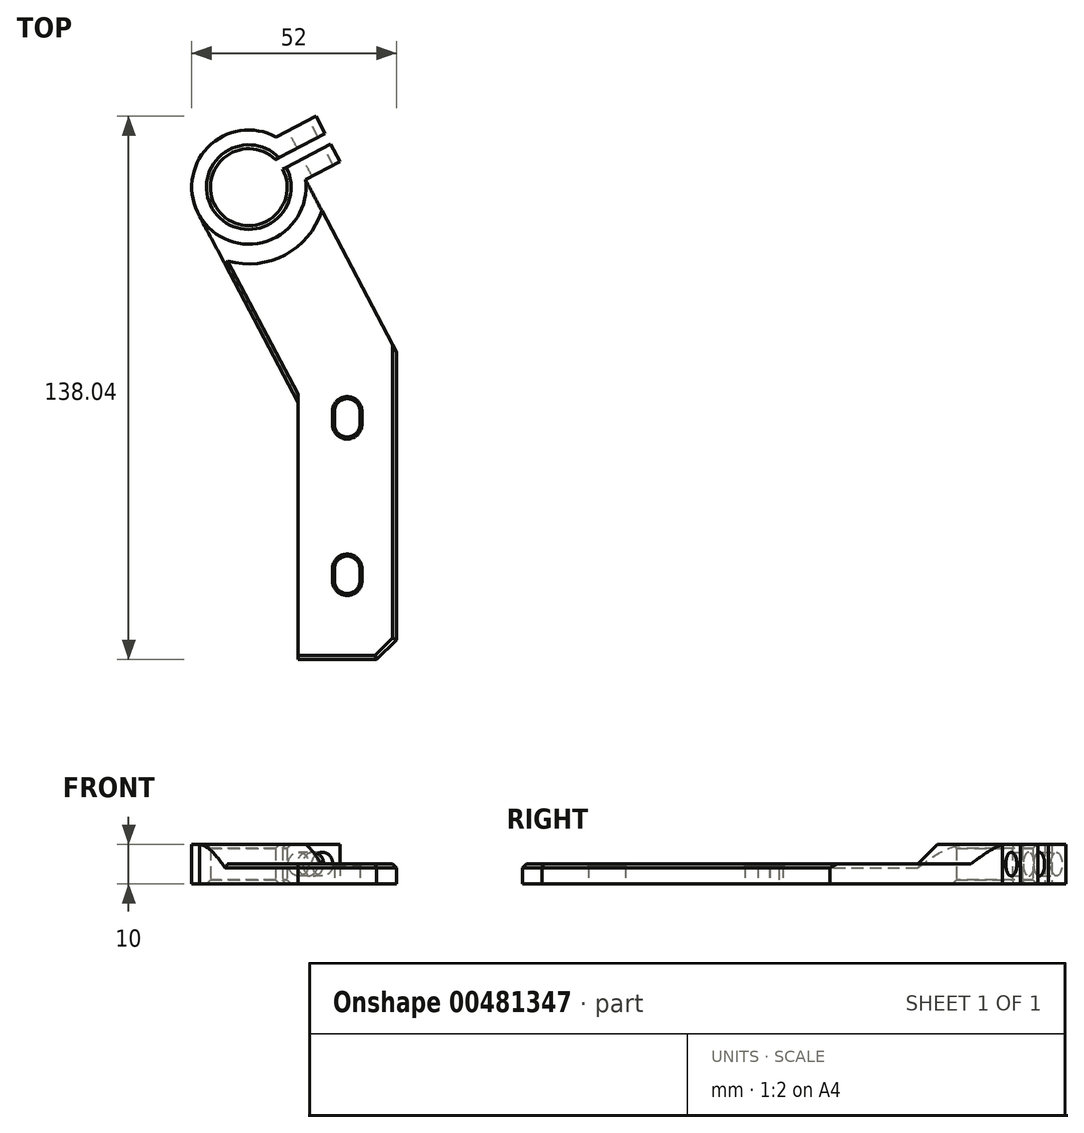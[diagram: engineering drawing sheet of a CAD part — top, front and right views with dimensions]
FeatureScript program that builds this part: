
annotation { "Feature Type Name" : "Feature", "Feature Type Description" : "" }
export const myFeature = defineFeature(function(context is Context, id is Id, definition is map)
    precondition{}
    {
        {
            var Q0;
            Q0=qCreatedBy(makeId("Top.planeOp"),FACE);
            var sketch = newSketch(context, id + "F0", { "sketchPlane" : qUnion([Q0])});
            skLineSegment(sketch, "E0.bottom", {"start": v(12.5, 40) * mm, "end": v(-12.5, 40) * mm});
            skLineSegment(sketch, "E0.top", {"start": v(12.5, -40) * mm, "end": v(-12.5, -40) * mm});
            skLineSegment(sketch, "E0.left", {"start": v(12.5, 40) * mm, "end": v(12.5, -40) * mm});
            skLineSegment(sketch, "E0.right", {"start": v(-12.5, 40) * mm, "end": v(-12.5, -40) * mm});
            skPoint(sketch, "E0.middle", {"position": v(0, 0) * mm});
            skLineSegment(sketch, "E1", {"start": v(0, -40) * mm, "end": v(0, -20) * mm});
            skPoint(sketch, "E1.endSnap0", {"position": v(0, -40) * mm});
            skCircle(sketch, "E2", {"center": v(0, -20) * mm, "radius": 3.25 * mm});
            skLineSegment(sketch, "E3", {"start": v(0, -20) * mm, "end": v(0, -17) * mm});
            skCircle(sketch, "E4", {"center": v(0, -17) * mm, "radius": 3.25 * mm});
            skLineSegment(sketch, "E5", {"start": v(3.25, -16.97) * mm, "end": v(3.25, -20) * mm});
            skLineSegment(sketch, "E6", {"start": v(-3.25, -17) * mm, "end": v(-3.25, -20) * mm});
            skLineSegment(sketch, "E7", {"start": v(0, -17) * mm, "end": v(0, 23) * mm});
            skCircle(sketch, "E8", {"center": v(0, 23) * mm, "radius": 3.25 * mm});
            skLineSegment(sketch, "E9", {"start": v(0, 23) * mm, "end": v(0, 19.75) * mm});
            skCircle(sketch, "E10", {"center": v(0, 19.75) * mm, "radius": 3.25 * mm});
            skLineSegment(sketch, "E11", {"start": v(3.25, 23.16) * mm, "end": v(3.25, 19.59) * mm});
            skLineSegment(sketch, "E12", {"start": v(-3.25, 19.75) * mm, "end": v(-3.24, 23.27) * mm});
            skLineSegment(sketch, "E13", {"start": v(0, 40) * mm, "end": v(-32.5, 40) * mm});
            skLineSegment(sketch, "E14.bottom", {"start": v(-12.5, 40) * mm, "end": v(-37.5, 40) * mm});
            skLineSegment(sketch, "E14.top", {"start": v(-12.5, 80) * mm, "end": v(-37.5, 80) * mm});
            skLineSegment(sketch, "E14.left", {"start": v(-12.5, 40) * mm, "end": v(-12.5, 80) * mm});
            skLineSegment(sketch, "E14.right", {"start": v(-37.5, 40) * mm, "end": v(-37.5, 80) * mm});
            skCircle(sketch, "E15", {"center": v(-25, 80) * mm, "radius": 14.5 * mm});
            skCircle(sketch, "E16", {"center": v(-25, 80) * mm, "radius": 9.75 * mm});
            skLineSegment(sketch, "E17", {"start": v(-12.5, 40) * mm, "end": v(-19.03, 32.43) * mm});
            skLineSegment(sketch, "E18", {"start": v(12.5, 40) * mm, "end": v(-12.18, 86.77) * mm});
            skLineSegment(sketch, "E19", {"start": v(-12.18, 86.77) * mm, "end": v(-37.82, 73.23) * mm});
            skLineSegment(sketch, "E20", {"start": v(-37.82, 73.23) * mm, "end": v(-12.5, 25.24) * mm});
            skLineSegment(sketch, "E21", {"start": v(-12.18, 86.77) * mm, "end": v(-4.22, 90.97) * mm});
            skLineSegment(sketch, "E22", {"start": v(-4.22, 90.97) * mm, "end": v(-5.62, 93.62) * mm});
            skLineSegment(sketch, "E23", {"start": v(-5.62, 93.62) * mm, "end": v(-13.85, 89.27) * mm});
            skLineSegment(sketch, "E24", {"start": v(-5.62, 93.62) * mm, "end": v(-7.95, 98.04) * mm});
            skLineSegment(sketch, "E25", {"start": v(-7.95, 98.04) * mm, "end": v(-18.04, 92.72) * mm});
            skLineSegment(sketch, "E26", {"start": v(-4.22, 90.97) * mm, "end": v(-1.88, 86.54) * mm});
            skLineSegment(sketch, "E27", {"start": v(-1.88, 86.54) * mm, "end": v(-9.84, 82.34) * mm});
            skLineSegment(sketch, "E28", {"start": v(-13.85, 89.27) * mm, "end": v(-18.2, 86.98) * mm});
            skLineSegment(sketch, "E29", {"start": v(-9.84, 82.34) * mm, "end": v(-10.63, 81.93) * mm});
            skSolve(sketch);
        }
        {
            var Q0;
            {var subQ4=sQuery(id+"F0.wireOp",EDGE,"E28");Q0=makeQuery(id+"F0.imprint","IMPRINT",FACE,{"disambiguationData":[TD([[makeQuery(id+"F0.imprint","IMPRINT",EDGE,{"derivedFrom":subQ4}),-1.0]])]});}
            var Q1;
            {var subQ0=sQuery(id+"F0.wireOp",EDGE,"E14.right");var subQ1=sQuery(id+"F0.wireOp",EDGE,"E14.top");var subQ2=makeQuery(id+"F0.imprint","INTERSECT",VERTEX,{"derivedFrom":[subQ1,subQ0]});Q1=makeQuery(id+"F0.imprint","IMPRINT",FACE,{"disambiguationData":[TD([[makeQuery(id+"F0.imprint","IMPRINT",EDGE,{"disambiguationData":[TD([[subQ2,1.0]])],"derivedFrom":subQ1}),1.0]])]});}
            var Q2;
            {var subQ1=sQuery(id+"F0.wireOp",EDGE,"E14.left");var subQ7=sQuery(id+"F0.wireOp",EDGE,"E14.top");var subQ8=makeQuery(id+"F0.imprint","INTERSECT",VERTEX,{"derivedFrom":[subQ7,subQ1]});Q2=makeQuery(id+"F0.imprint","IMPRINT",FACE,{"disambiguationData":[TD([[makeQuery(id+"F0.imprint","IMPRINT",EDGE,{"disambiguationData":[TD([[subQ8,-1.0]])],"derivedFrom":subQ7}),1.0]])]});}
            var Q3;
            {var subQ0=sQuery(id+"F0.wireOp",EDGE,"E23");Q3=makeQuery(id+"F0.imprint","IMPRINT",FACE,{"disambiguationData":[TD([[makeQuery(id+"F0.imprint","IMPRINT",EDGE,{"derivedFrom":subQ0}),-1.0]])]});}
            var Q4;
            {var subQ1=sQuery(id+"F0.wireOp",EDGE,"E14.top");var subQ5=sQuery(id+"F0.wireOp",EDGE,"E14.left");var subQ6=makeQuery(id+"F0.imprint","INTERSECT",VERTEX,{"derivedFrom":[subQ1,subQ5]});Q4=makeQuery(id+"F0.imprint","IMPRINT",FACE,{"disambiguationData":[TD([[makeQuery(id+"F0.imprint","IMPRINT",EDGE,{"disambiguationData":[TD([[subQ6,-1.0]])],"derivedFrom":subQ1}),-1.0]])]});}
            var Q5;
            {var subQ0=sQuery(id+"F0.wireOp",EDGE,"E21");Q5=makeQuery(id+"F0.imprint","IMPRINT",FACE,{"disambiguationData":[TD([[makeQuery(id+"F0.imprint","IMPRINT",EDGE,{"derivedFrom":subQ0}),-1.0]])]});}
            var Q6;
            {var subQ0=sQuery(id+"F0.wireOp",EDGE,"E20");var subQ1=sQuery(id+"F0.wireOp",EDGE,"E14.right");var subQ2=makeQuery(id+"F0.imprint","INTERSECT",VERTEX,{"derivedFrom":[subQ1,subQ0]});Q6=makeQuery(id+"F0.imprint","IMPRINT",FACE,{"disambiguationData":[TD([[makeQuery(id+"F0.imprint","IMPRINT",EDGE,{"disambiguationData":[TD([[subQ2,-1.0]])],"derivedFrom":subQ1}),-1.0]])]});}
            var Q7;
            {var subQ6=sQuery(id+"F0.wireOp",EDGE,"E0.bottom");Q7=makeQuery(id+"F0.imprint","IMPRINT",FACE,{"disambiguationData":[TD([[makeQuery(id+"F0.imprint","IMPRINT",EDGE,{"derivedFrom":subQ6}),-1.0]])]});}
            var Q8;
            {var subQ1=sQuery(id+"F0.wireOp",EDGE,"E0.right");var subQ3=sQuery(id+"F0.wireOp",EDGE,"E20");var subQ4=makeQuery(id+"F0.imprint","INTERSECT",VERTEX,{"derivedFrom":[subQ1,subQ3]});Q8=makeQuery(id+"F0.imprint","IMPRINT",FACE,{"disambiguationData":[TD([[makeQuery(id+"F0.imprint","IMPRINT",EDGE,{"disambiguationData":[TD([[subQ4,1.0]])],"derivedFrom":subQ3}),1.0]])]});}
            var Q9;
            Q9=makeQuery(id+"F0.imprint","IMPRINT",FACE,{"disambiguationData":[TD([[makeQuery(id+"F0.imprint","IMPRINT",EDGE,{"derivedFrom":sQuery(id+"F0.wireOp",EDGE,"E0.bottom")}),1.0]])]});
            var Q10;
            {var subQ0=sQuery(id+"F0.wireOp",EDGE,"E17");var subQ3=sQuery(id+"F0.wireOp",EDGE,"E20");var subQ5=makeQuery(id+"F0.imprint","INTERSECT",VERTEX,{"derivedFrom":[subQ0,subQ3]});Q10=makeQuery(id+"F0.imprint","IMPRINT",FACE,{"disambiguationData":[TD([[makeQuery(id+"F0.imprint","IMPRINT",EDGE,{"disambiguationData":[TD([[subQ5,1.0]])],"derivedFrom":subQ3}),1.0]])]});}
            var Q11;
            {var subQ0=sQuery(id+"F0.wireOp",EDGE,"Hvk5iKsL-lssr-s4Mr-CGHE-9GIf69tuhGeW");Q11=makeQuery(id+"F0.imprint","IMPRINT",FACE,{"disambiguationData":[TD([[makeQuery(id+"F0.imprint","IMPRINT",EDGE,{"derivedFrom":subQ0}),-1.0]])]});}
            var Q12;
            {var subQ0=sQuery(id+"F0.wireOp",EDGE,"E15");var subQ1=sQuery(id+"F0.wireOp",EDGE,"E14.right");var subQ2=makeQuery(id+"F0.imprint","INTERSECT",VERTEX,{"derivedFrom":[subQ1,subQ0]});Q12=makeQuery(id+"F0.imprint","IMPRINT",FACE,{"disambiguationData":[TD([[makeQuery(id+"F0.imprint","IMPRINT",EDGE,{"disambiguationData":[TD([[subQ2,-1.0]])],"derivedFrom":subQ1}),1.0]])]});}
            var Q13;
            {var subQ3=sQuery(id+"F0.wireOp",EDGE,"E29");Q13=makeQuery(id+"F0.imprint","IMPRINT",FACE,{"disambiguationData":[TD([[makeQuery(id+"F0.imprint","IMPRINT",EDGE,{"derivedFrom":subQ3}),-1.0]])]});}
            extrude(context, id + "F1", {"entities" : qUnion([Q0, Q1, Q2, Q3, Q4, Q5, Q6, Q7, Q8, Q9, Q10, Q11, Q12, Q13]), "depth" : 5 * mm});
        }
        {
            var Q0;
            {var subQ2=sQuery(id+"F0.wireOp",EDGE,"E14.left");var subQ4=sQuery(id+"F0.wireOp",EDGE,"E14.top");var subQ5=makeQuery(id+"F0.imprint","INTERSECT",VERTEX,{"derivedFrom":[subQ4,subQ2]});Q0=makeQuery(id+"F0.imprint","IMPRINT",FACE,{"disambiguationData":[TD([[makeQuery(id+"F0.imprint","IMPRINT",EDGE,{"disambiguationData":[TD([[subQ5,-1.0]])],"derivedFrom":subQ4}),-1.0]])]});}
            var Q1;
            {var subQ0=sQuery(id+"F0.wireOp",EDGE,"E21");Q1=makeQuery(id+"F0.imprint","IMPRINT",FACE,{"disambiguationData":[TD([[makeQuery(id+"F0.imprint","IMPRINT",EDGE,{"derivedFrom":subQ0}),-1.0]])]});}
            var Q2;
            {var subQ0=sQuery(id+"F0.wireOp",EDGE,"E23");Q2=makeQuery(id+"F0.imprint","IMPRINT",FACE,{"disambiguationData":[TD([[makeQuery(id+"F0.imprint","IMPRINT",EDGE,{"derivedFrom":subQ0}),-1.0]])]});}
            var Q3;
            {var subQ0=sQuery(id+"F0.wireOp",EDGE,"E28");Q3=makeQuery(id+"F0.imprint","IMPRINT",FACE,{"disambiguationData":[TD([[makeQuery(id+"F0.imprint","IMPRINT",EDGE,{"derivedFrom":subQ0}),-1.0]])]});}
            var Q4;
            {var subQ3=sQuery(id+"F0.wireOp",EDGE,"E29");Q4=makeQuery(id+"F0.imprint","IMPRINT",FACE,{"disambiguationData":[TD([[makeQuery(id+"F0.imprint","IMPRINT",EDGE,{"derivedFrom":subQ3}),-1.0]])]});}
            var Q5;
            {var subQ5=sQuery(id+"F0.wireOp",EDGE,"E14.left");var subQ7=sQuery(id+"F0.wireOp",EDGE,"E14.top");var subQ8=makeQuery(id+"F0.imprint","INTERSECT",VERTEX,{"derivedFrom":[subQ7,subQ5]});Q5=makeQuery(id+"F0.imprint","IMPRINT",FACE,{"disambiguationData":[TD([[makeQuery(id+"F0.imprint","IMPRINT",EDGE,{"disambiguationData":[TD([[subQ8,-1.0]])],"derivedFrom":subQ7}),1.0]])]});}
            var Q6;
            {var subQ0=sQuery(id+"F0.wireOp",EDGE,"E14.right");var subQ1=sQuery(id+"F0.wireOp",EDGE,"E14.top");var subQ2=makeQuery(id+"F0.imprint","INTERSECT",VERTEX,{"derivedFrom":[subQ1,subQ0]});Q6=makeQuery(id+"F0.imprint","IMPRINT",FACE,{"disambiguationData":[TD([[makeQuery(id+"F0.imprint","IMPRINT",EDGE,{"disambiguationData":[TD([[subQ2,1.0]])],"derivedFrom":subQ1}),1.0]])]});}
            var Q7;
            {var subQ0=sQuery(id+"F0.wireOp",EDGE,"E15");var subQ1=sQuery(id+"F0.wireOp",EDGE,"E14.right");var subQ2=makeQuery(id+"F0.imprint","INTERSECT",VERTEX,{"derivedFrom":[subQ1,subQ0]});Q7=makeQuery(id+"F0.imprint","IMPRINT",FACE,{"disambiguationData":[TD([[makeQuery(id+"F0.imprint","IMPRINT",EDGE,{"disambiguationData":[TD([[subQ2,-1.0]])],"derivedFrom":subQ1}),1.0]])]});}
            extrude(context, id + "F2", {"entities" : qUnion([Q0, Q1, Q2, Q3, Q4, Q5, Q6, Q7]), "operationType" : NewBodyOperationType.ADD, "depth" : 10 * mm});
        }
        {
            var Q0;
            {var subQ0=sQuery(id+"F0.wireOp",EDGE,"E25");Q0=makeQuery(id+"F2.boolean.opBoolean","MERGE",FACE,{"derivedFrom":[makeQuery(id+"F1.opExtrude","SWEPT_FACE",FACE,{"disambiguationData":[OSD([subQ0])]}),makeQuery(id+"F2.opExtrude","SWEPT_FACE",FACE,{"disambiguationData":[OSD([subQ0])]})]});}
            var sketch = newSketch(context, id + "F3", { "sketchPlane" : qUnion([Q0])});
            skPoint(sketch, "E30.centerSnap0", {"position": v(-33.02, 0) * mm});
            skPoint(sketch, "E30.centerSnap1", {"position": v(-38.72, 5) * mm});
            skLineSegment(sketch, "E31", {"start": v(-38.72, 5) * mm, "end": v(-33.72, 5) * mm});
            skCircle(sketch, "E32", {"center": v(-33.72, 5) * mm, "radius": 3 * mm});
            skSolve(sketch);
        }
        {
            var Q0;
            Q0=makeQuery(id+"F3.imprint","IMPRINT",FACE,{"disambiguationData":[TD([[makeQuery(id+"F3.imprint","IMPRINT",EDGE,{"derivedFrom":sQuery(id+"F3.wireOp",EDGE,"E30")}),1.0]])]});
            var Q1;
            Q1=makeQuery(id+"F3.imprint","IMPRINT",FACE,{"disambiguationData":[TD([[makeQuery(id+"F3.imprint","IMPRINT",EDGE,{"derivedFrom":sQuery(id+"F3.wireOp",EDGE,"E32")}),1.0]])]});
            extrude(context, id + "F4", {"entities" : qUnion([Q0, Q1]), "operationType" : NewBodyOperationType.REMOVE, "oppositeDirection" : true, "depth" : 13 * mm});
        }
        {
            var Q0;
            {var subQ0=sQuery(id+"F0.wireOp",EDGE,"E27");Q0=makeQuery(id+"F2.boolean.opBoolean","MERGE",FACE,{"derivedFrom":[makeQuery(id+"F1.opExtrude","SWEPT_FACE",FACE,{"disambiguationData":[OSD([subQ0])]}),makeQuery(id+"F2.opExtrude","SWEPT_FACE",FACE,{"disambiguationData":[OSD([subQ0,sQuery(id+"F0.wireOp",EDGE,"E29")])]})]});}
            var sketch = newSketch(context, id + "F5", { "sketchPlane" : qUnion([Q0])});
            skLineSegment(sketch, "E33", {"start": v(28.83, 5) * mm, "end": v(28.83, 0) * mm});
            skLineSegment(sketch, "E34", {"start": v(28.83, 0) * mm, "end": v(29.72, 0) * mm});
            skLineSegment(sketch, "E35", {"start": v(29.72, 0) * mm, "end": v(29.72, 5) * mm});
            skLineSegment(sketch, "E36", {"start": v(29.72, 5) * mm, "end": v(28.83, 5) * mm});
            skSolve(sketch);
        }
        {
            var Q0;
            Q0 = qSketchRegion(id + "F5", true);
            extrude(context, id + "F6", {"entities" : qUnion([Q0]), "operationType" : NewBodyOperationType.REMOVE, "depth" : 52.8 * mm});
        }
        {
            var Q0;
            Q0=makeQuery(id+"F1.opExtrude","SWEPT_EDGE",EDGE,{"disambiguationData":[OSD([sQuery(id+"F0.wireOp",EDGE,"Hvk5iKsL-lssr-s4Mr-CGHE-9GIf69tuhGeW"),sQuery(id+"F0.wireOp",EDGE,"ejzlW1ob-3sVt-pXpa-F90c-4b1ble51zeoF")])]});
            var Q1;
            Q1=makeQuery(id+"F1.opExtrude","SWEPT_EDGE",EDGE,{"disambiguationData":[OSD([sQuery(id+"F0.wireOp",EDGE,"E0.top"),sQuery(id+"F0.wireOp",EDGE,"E0.left")])]});
            chamfer(context, id + "F7", {"entities" : qUnion([Q0, Q1]), "width" : 5 * mm, "tangentPropagation" : true});
        }
        {
            var Q0;
            {var subQ0=sQuery(id+"F0.wireOp",EDGE,"E15");Q0=makeQuery(id+"F2.boolean.opBoolean","INTERSECT",EDGE,{"derivedFrom":[makeQuery(id+"F1.opExtrude","CAP_FACE",FACE,{"disambiguationData":[OSD([sQuery(id+"F0.wireOp",EDGE,"E0.top"),sQuery(id+"F0.wireOp",EDGE,"E0.left"),sQuery(id+"F0.wireOp",EDGE,"E2"),sQuery(id+"F0.wireOp",EDGE,"E4"),sQuery(id+"F0.wireOp",EDGE,"E5"),sQuery(id+"F0.wireOp",EDGE,"E6"),sQuery(id+"F0.wireOp",EDGE,"E8"),sQuery(id+"F0.wireOp",EDGE,"E10"),sQuery(id+"F0.wireOp",EDGE,"E11"),sQuery(id+"F0.wireOp",EDGE,"E12"),sQuery(id+"F0.wireOp",EDGE,"E14.right"),subQ0,sQuery(id+"F0.wireOp",EDGE,"E16"),sQuery(id+"F0.wireOp",EDGE,"E18"),sQuery(id+"F0.wireOp",EDGE,"E19"),sQuery(id+"F0.wireOp",EDGE,"E20"),sQuery(id+"F0.wireOp",EDGE,"E21"),sQuery(id+"F0.wireOp",EDGE,"E23"),sQuery(id+"F0.wireOp",EDGE,"E24"),sQuery(id+"F0.wireOp",EDGE,"E25"),sQuery(id+"F0.wireOp",EDGE,"E26"),sQuery(id+"F0.wireOp",EDGE,"E27"),sQuery(id+"F0.wireOp",EDGE,"E28"),sQuery(id+"F0.wireOp",EDGE,"Hvk5iKsL-lssr-s4Mr-CGHE-9GIf69tuhGeW"),sQuery(id+"F0.wireOp",EDGE,"ejzlW1ob-3sVt-pXpa-F90c-4b1ble51zeoF")])],"isStart":false}),makeQuery(id+"F2.opExtrude","SWEPT_FACE",FACE,{"disambiguationData":[OSD([subQ0])]})]});}
            chamfer(context, id + "F8", {"entities" : qUnion([Q0]), "width" : 5 * mm, "tangentPropagation" : true});
        }
        {
            var Q0;
            Q0=makeQuery(id+"F1.opExtrude","CAP_EDGE",EDGE,{"disambiguationData":[OSD([sQuery(id+"F0.wireOp",EDGE,"ejzlW1ob-3sVt-pXpa-F90c-4b1ble51zeoF")])],"isStart":false});
            var Q1;
            Q1=makeQuery(id+"F1.opExtrude","CAP_EDGE",EDGE,{"disambiguationData":[OSD([sQuery(id+"F0.wireOp",EDGE,"E0.left")])],"isStart":false});
            var Q2;
            Q2=makeQuery(id+"F1.opExtrude","CAP_EDGE",EDGE,{"disambiguationData":[OSD([sQuery(id+"F0.wireOp",EDGE,"E0.top"),sQuery(id+"F0.wireOp",EDGE,"Hvk5iKsL-lssr-s4Mr-CGHE-9GIf69tuhGeW")])],"isStart":false});
            var Q3;
            {var subQ0=sQuery(id+"F0.wireOp",EDGE,"ejzlW1ob-3sVt-pXpa-F90c-4b1ble51zeoF");var subQ1=sQuery(id+"F0.wireOp",EDGE,"Hvk5iKsL-lssr-s4Mr-CGHE-9GIf69tuhGeW");Q3=makeQuery(id+"F7.opChamfer","BLEND_EDGE",EDGE,{"blendedFrom":[makeQuery(id+"F1.opExtrude","SWEPT_EDGE",EDGE,{"disambiguationData":[OSD([subQ1,subQ0])]}),makeQuery(id+"F1.opExtrude","CAP_FACE",FACE,{"disambiguationData":[OSD([sQuery(id+"F0.wireOp",EDGE,"E0.top"),sQuery(id+"F0.wireOp",EDGE,"E0.left"),sQuery(id+"F0.wireOp",EDGE,"E2"),sQuery(id+"F0.wireOp",EDGE,"E4"),sQuery(id+"F0.wireOp",EDGE,"E5"),sQuery(id+"F0.wireOp",EDGE,"E6"),sQuery(id+"F0.wireOp",EDGE,"E8"),sQuery(id+"F0.wireOp",EDGE,"E10"),sQuery(id+"F0.wireOp",EDGE,"E11"),sQuery(id+"F0.wireOp",EDGE,"E12"),sQuery(id+"F0.wireOp",EDGE,"E14.right"),sQuery(id+"F0.wireOp",EDGE,"E15"),sQuery(id+"F0.wireOp",EDGE,"E16"),sQuery(id+"F0.wireOp",EDGE,"E18"),sQuery(id+"F0.wireOp",EDGE,"E19"),sQuery(id+"F0.wireOp",EDGE,"E20"),sQuery(id+"F0.wireOp",EDGE,"E21"),sQuery(id+"F0.wireOp",EDGE,"E23"),sQuery(id+"F0.wireOp",EDGE,"E24"),sQuery(id+"F0.wireOp",EDGE,"E25"),sQuery(id+"F0.wireOp",EDGE,"E26"),sQuery(id+"F0.wireOp",EDGE,"E27"),sQuery(id+"F0.wireOp",EDGE,"E28"),subQ1,subQ0])],"isStart":false})],"blendedInto":[makeQuery(id+"F1.opExtrude","CAP_FACE",FACE,{"disambiguationData":[OSD([sQuery(id+"F0.wireOp",EDGE,"E0.top"),sQuery(id+"F0.wireOp",EDGE,"E0.left"),sQuery(id+"F0.wireOp",EDGE,"E2"),sQuery(id+"F0.wireOp",EDGE,"E4"),sQuery(id+"F0.wireOp",EDGE,"E5"),sQuery(id+"F0.wireOp",EDGE,"E6"),sQuery(id+"F0.wireOp",EDGE,"E8"),sQuery(id+"F0.wireOp",EDGE,"E10"),sQuery(id+"F0.wireOp",EDGE,"E11"),sQuery(id+"F0.wireOp",EDGE,"E12"),sQuery(id+"F0.wireOp",EDGE,"E14.right"),sQuery(id+"F0.wireOp",EDGE,"E15"),sQuery(id+"F0.wireOp",EDGE,"E16"),sQuery(id+"F0.wireOp",EDGE,"E18"),sQuery(id+"F0.wireOp",EDGE,"E19"),sQuery(id+"F0.wireOp",EDGE,"E20"),sQuery(id+"F0.wireOp",EDGE,"E21"),sQuery(id+"F0.wireOp",EDGE,"E23"),sQuery(id+"F0.wireOp",EDGE,"E24"),sQuery(id+"F0.wireOp",EDGE,"E25"),sQuery(id+"F0.wireOp",EDGE,"E26"),sQuery(id+"F0.wireOp",EDGE,"E27"),sQuery(id+"F0.wireOp",EDGE,"E28"),subQ1,subQ0])],"isStart":false})]});}
            var Q4;
            {var subQ0=sQuery(id+"F0.wireOp",EDGE,"E0.left");var subQ1=sQuery(id+"F0.wireOp",EDGE,"E0.top");Q4=makeQuery(id+"F7.opChamfer","BLEND_EDGE",EDGE,{"blendedFrom":[makeQuery(id+"F1.opExtrude","SWEPT_EDGE",EDGE,{"disambiguationData":[OSD([subQ1,subQ0])]}),makeQuery(id+"F1.opExtrude","CAP_FACE",FACE,{"disambiguationData":[OSD([subQ1,subQ0,sQuery(id+"F0.wireOp",EDGE,"E2"),sQuery(id+"F0.wireOp",EDGE,"E4"),sQuery(id+"F0.wireOp",EDGE,"E5"),sQuery(id+"F0.wireOp",EDGE,"E6"),sQuery(id+"F0.wireOp",EDGE,"E8"),sQuery(id+"F0.wireOp",EDGE,"E10"),sQuery(id+"F0.wireOp",EDGE,"E11"),sQuery(id+"F0.wireOp",EDGE,"E12"),sQuery(id+"F0.wireOp",EDGE,"E14.right"),sQuery(id+"F0.wireOp",EDGE,"E15"),sQuery(id+"F0.wireOp",EDGE,"E16"),sQuery(id+"F0.wireOp",EDGE,"E18"),sQuery(id+"F0.wireOp",EDGE,"E19"),sQuery(id+"F0.wireOp",EDGE,"E20"),sQuery(id+"F0.wireOp",EDGE,"E21"),sQuery(id+"F0.wireOp",EDGE,"E23"),sQuery(id+"F0.wireOp",EDGE,"E24"),sQuery(id+"F0.wireOp",EDGE,"E25"),sQuery(id+"F0.wireOp",EDGE,"E26"),sQuery(id+"F0.wireOp",EDGE,"E27"),sQuery(id+"F0.wireOp",EDGE,"E28"),sQuery(id+"F0.wireOp",EDGE,"Hvk5iKsL-lssr-s4Mr-CGHE-9GIf69tuhGeW"),sQuery(id+"F0.wireOp",EDGE,"ejzlW1ob-3sVt-pXpa-F90c-4b1ble51zeoF")])],"isStart":false})],"blendedInto":[makeQuery(id+"F1.opExtrude","CAP_FACE",FACE,{"disambiguationData":[OSD([subQ1,subQ0,sQuery(id+"F0.wireOp",EDGE,"E2"),sQuery(id+"F0.wireOp",EDGE,"E4"),sQuery(id+"F0.wireOp",EDGE,"E5"),sQuery(id+"F0.wireOp",EDGE,"E6"),sQuery(id+"F0.wireOp",EDGE,"E8"),sQuery(id+"F0.wireOp",EDGE,"E10"),sQuery(id+"F0.wireOp",EDGE,"E11"),sQuery(id+"F0.wireOp",EDGE,"E12"),sQuery(id+"F0.wireOp",EDGE,"E14.right"),sQuery(id+"F0.wireOp",EDGE,"E15"),sQuery(id+"F0.wireOp",EDGE,"E16"),sQuery(id+"F0.wireOp",EDGE,"E18"),sQuery(id+"F0.wireOp",EDGE,"E19"),sQuery(id+"F0.wireOp",EDGE,"E20"),sQuery(id+"F0.wireOp",EDGE,"E21"),sQuery(id+"F0.wireOp",EDGE,"E23"),sQuery(id+"F0.wireOp",EDGE,"E24"),sQuery(id+"F0.wireOp",EDGE,"E25"),sQuery(id+"F0.wireOp",EDGE,"E26"),sQuery(id+"F0.wireOp",EDGE,"E27"),sQuery(id+"F0.wireOp",EDGE,"E28"),sQuery(id+"F0.wireOp",EDGE,"Hvk5iKsL-lssr-s4Mr-CGHE-9GIf69tuhGeW"),sQuery(id+"F0.wireOp",EDGE,"ejzlW1ob-3sVt-pXpa-F90c-4b1ble51zeoF")])],"isStart":false})]});}
            var Q5;
            Q5=makeQuery(id+"F1.opExtrude","CAP_EDGE",EDGE,{"disambiguationData":[OSD([sQuery(id+"F0.wireOp",EDGE,"E20")])],"isStart":false});
            var Q6;
            Q6=makeQuery(id+"F6.boolean.opBoolean","COPY",EDGE,{"derivedFrom":makeQuery(id+"F6.opExtrude","SWEPT_EDGE",EDGE,{"disambiguationData":[OSD([sQuery(id+"F0.wireOp",EDGE,"E15"),sQuery(id+"F0.wireOp",EDGE,"E29"),sQuery(id+"F5.wireOp",EDGE,"E33"),sQuery(id+"F5.wireOp",EDGE,"E36")])]})});
            var Q7;
            Q7=makeQuery(id+"F1.opExtrude","CAP_EDGE",EDGE,{"disambiguationData":[OSD([sQuery(id+"F0.wireOp",EDGE,"E16")])],"isStart":true});
            var Q8;
            Q8=makeQuery(id+"F2.opExtrude","CAP_EDGE",EDGE,{"disambiguationData":[OSD([sQuery(id+"F0.wireOp",EDGE,"E16")])],"isStart":false});
            chamfer(context, id + "F9", {"entities" : qUnion([Q0, Q1, Q2, Q3, Q4, Q5, Q6, Q7, Q8]), "width" : 1 * mm, "tangentPropagation" : true});
        }
        {
            var Q0;
            Q0=makeQuery(id+"F1.opExtrude","CAP_EDGE",EDGE,{"disambiguationData":[OSD([sQuery(id+"F0.wireOp",EDGE,"E10")])],"isStart":false});
            var Q1;
            Q1=makeQuery(id+"F1.opExtrude","CAP_EDGE",EDGE,{"disambiguationData":[OSD([sQuery(id+"F0.wireOp",EDGE,"E4")])],"isStart":false});
            var Q2;
            Q2=makeQuery(id+"F1.opExtrude","CAP_EDGE",EDGE,{"disambiguationData":[OSD([sQuery(id+"F0.wireOp",EDGE,"E5")])],"isStart":false});
            var Q3;
            Q3=makeQuery(id+"F1.opExtrude","CAP_EDGE",EDGE,{"disambiguationData":[OSD([sQuery(id+"F0.wireOp",EDGE,"E8")])],"isStart":false});
            var Q4;
            Q4=makeQuery(id+"F1.opExtrude","CAP_EDGE",EDGE,{"disambiguationData":[OSD([sQuery(id+"F0.wireOp",EDGE,"E11")])],"isStart":false});
            var Q5;
            Q5=makeQuery(id+"F1.opExtrude","CAP_EDGE",EDGE,{"disambiguationData":[OSD([sQuery(id+"F0.wireOp",EDGE,"E12")])],"isStart":false});
            var Q6;
            Q6=makeQuery(id+"F1.opExtrude","CAP_EDGE",EDGE,{"disambiguationData":[OSD([sQuery(id+"F0.wireOp",EDGE,"E6")])],"isStart":false});
            var Q7;
            Q7=makeQuery(id+"F1.opExtrude","CAP_EDGE",EDGE,{"disambiguationData":[OSD([sQuery(id+"F0.wireOp",EDGE,"E2")])],"isStart":false});
            var Q8;
            Q8=makeQuery(id+"F4.boolean.opBoolean","COPY",EDGE,{"derivedFrom":makeQuery(id+"F4.opExtrude","CAP_EDGE",EDGE,{"disambiguationData":[OSD([sQuery(id+"F3.wireOp",EDGE,"E32")])],"isStart":true})});
            var Q9;
            Q9=makeQuery(id+"F4.boolean.opBoolean","COPY",EDGE,{"derivedFrom":makeQuery(id+"F4.opExtrude","CAP_EDGE",EDGE,{"disambiguationData":[OSD([sQuery(id+"F3.wireOp",EDGE,"E32")])],"isStart":false})});
            chamfer(context, id + "F10", {"entities" : qUnion([Q0, Q1, Q2, Q3, Q4, Q5, Q6, Q7, Q8, Q9]), "width" : .5 * mm, "tangentPropagation" : true});
        }
    });
